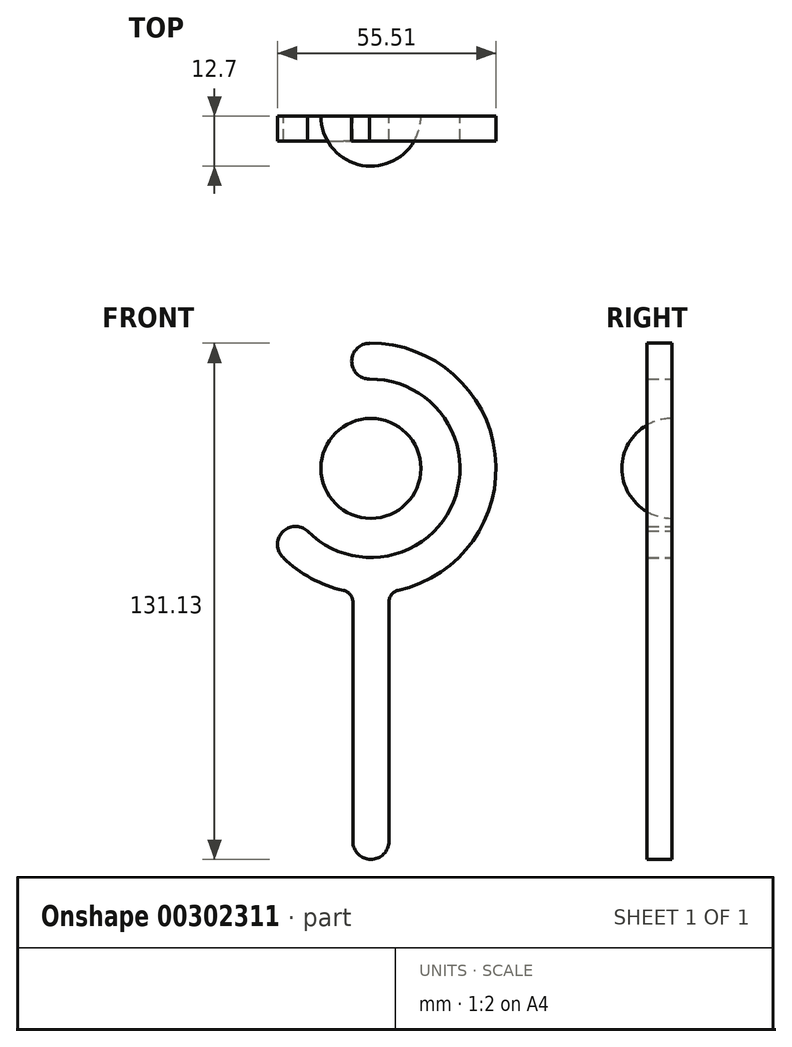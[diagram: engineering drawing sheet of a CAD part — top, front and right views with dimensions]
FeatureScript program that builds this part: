
annotation { "Feature Type Name" : "Feature", "Feature Type Description" : "" }
export const myFeature = defineFeature(function(context is Context, id is Id, definition is map)
    precondition{}
    {
        {
            var Q0;
            Q0=qCreatedBy(makeId("Front.planeOp"),FACE);
            var sketch = newSketch(context, id + "F0", { "sketchPlane" : qUnion([Q0])});
            skPoint(sketch, "E0.middle", {"position": v(0, 0) * mm});
            skCircle(sketch, "E1", {"center": v(0, 51.44) * mm, "radius": 12.7 * mm});
            skArc(sketch, "E2", {"start": v(-16.1, 35.5) * mm, "mid": v(-16.05, 35.46) * mm, "end": v(-16, 35.4) * mm});
            skArc(sketch, "E3", {"start": v(-0.33, 74.08) * mm, "mid": v(-20.96, 60) * mm, "end": v(-16.1, 35.5) * mm, "construction": true});
            skArc(sketch, "E4", {"start": v(-0.33, 83.22) * mm, "mid": v(-29.5, 63.3) * mm, "end": v(-22.24, 28.72) * mm, "construction": true});
            skArc(sketch, "E5", {"start": v(-22.24, 28.72) * mm, "mid": v(-15.17, 23.5) * mm, "end": v(-6.95, 20.42) * mm});
            skLineSegment(sketch, "E6", {"start": v(-0.33, 83.22) * mm, "end": v(-0.33, 74.08) * mm});
            skLineSegment(sketch, "E7", {"start": v(-16.1, 35.5) * mm, "end": v(-22.24, 28.72) * mm});
            skLineSegment(sketch, "E8.bottom", {"start": v(4.57, -43.34) * mm, "end": v(-4.57, -43.34) * mm});
            skLineSegment(sketch, "E8.left", {"start": v(4.57, -43.34) * mm, "end": v(4.57, -43.34) * mm});
            skLineSegment(sketch, "E8.right", {"start": v(-4.57, -43.34) * mm, "end": v(-4.57, 17.44) * mm});
            skPoint(sketch, "E8.middle", {"position": v(0, -11.28) * mm});
            skLineSegment(sketch, "E9", {"start": v(0, 64.14) * mm, "end": v(0, 38.74) * mm});
            skArc(sketch, "E10", {"start": v(6.95, 20.42) * mm, "mid": v(31.58, 55.1) * mm, "end": v(-0.33, 83.22) * mm});
            skPoint(sketch, "E11.visualSharp", {"position": v(-4.57, 19.98) * mm});
            skArc(sketch, "E11.filletArc", {"start": v(-4.57, 17.44) * mm, "mid": v(-5.24, 19.35) * mm, "end": v(-6.95, 20.42) * mm});
            skPoint(sketch, "E12.visualSharp", {"position": v(4.57, 19.98) * mm});
            skArc(sketch, "E12.filletArc", {"start": v(6.95, 20.42) * mm, "mid": v(5.24, 19.35) * mm, "end": v(4.57, 17.44) * mm});
            skArc(sketch, "E13", {"start": v(-16, 35.4) * mm, "mid": v(20.99, 42.93) * mm, "end": v(-0.33, 74.08) * mm});
            skLineSegment(sketch, "E14", {"start": v(-15.5, 29.41) * mm, "end": v(-15.5, 29.41) * mm});
            skArc(sketch, "E15", {"start": v(-16.12, 35.49) * mm, "mid": v(-22.54, 35.16) * mm, "end": v(-22.22, 28.74) * mm});
            skArc(sketch, "E16", {"start": v(-0.33, 83.2) * mm, "mid": v(-4.88, 78.65) * mm, "end": v(-0.33, 74.1) * mm});
            skLineSegment(sketch, "E17", {"start": v(4.22, 78.62) * mm, "end": v(4.22, 78.62) * mm});
            skArc(sketch, "E18", {"start": v(-4.57, -43.34) * mm, "mid": v(0, -47.9) * mm, "end": v(4.57, -43.34) * mm});
            skLineSegment(sketch, "E19", {"start": v(0.04, -38.77) * mm, "end": v(0.04, -38.77) * mm});
            skLineSegment(sketch, "E20", {"start": v(4.57, -43.34) * mm, "end": v(4.57, 17.44) * mm});
            skSolve(sketch);
        }
        {
            var Q0;
            {var subQ0=sQuery(id+"F0.wireOp",EDGE,"E9");Q0=makeQuery(id+"F0.imprint","IMPRINT",FACE,{"disambiguationData":[TD([[makeQuery(id+"F0.imprint","IMPRINT",EDGE,{"derivedFrom":subQ0}),1.0]])]});}
            var Q1;
            Q1=sQuery(id+"F0.wireOp",EDGE,"E9");
            revolve(context, id + "F1", {"entities" : qUnion([Q0]), "axis" : qUnion([Q1]), "revolveType" : RevolveType.TWO_DIRECTIONS, "angle" : 180 * degree, "angleBack" : 360 * degree});
        }
        {
            var Q0;
            {var subQ5=sQuery(id+"F0.wireOp",EDGE,"E2");Q0=makeQuery(id+"F0.imprint","IMPRINT",FACE,{"disambiguationData":[TD([[makeQuery(id+"F0.imprint","IMPRINT",EDGE,{"derivedFrom":subQ5}),-1.0]])]});}
            var Q1;
            {var subQ0=sQuery(id+"F0.wireOp",EDGE,"E15");Q1=makeQuery(id+"F0.imprint","IMPRINT",FACE,{"disambiguationData":[TD([[makeQuery(id+"F0.imprint","IMPRINT",EDGE,{"derivedFrom":subQ0}),1.0]])]});}
            var Q2;
            {var subQ0=sQuery(id+"F0.wireOp",EDGE,"E16");Q2=makeQuery(id+"F0.imprint","IMPRINT",FACE,{"disambiguationData":[TD([[makeQuery(id+"F0.imprint","IMPRINT",EDGE,{"derivedFrom":subQ0}),1.0]])]});}
            var Q3;
            Q3=makeQuery(id+"F0.imprint","IMPRINT",FACE,{"disambiguationData":[TD([[makeQuery(id+"F0.imprint","IMPRINT",EDGE,{"derivedFrom":sQuery(id+"F0.wireOp",EDGE,"E8.bottom")}),1.0]])]});
            extrude(context, id + "F2", {"entities" : qUnion([Q0, Q1, Q2, Q3]), "depth" : 6.35 * mm});
        }
    });
